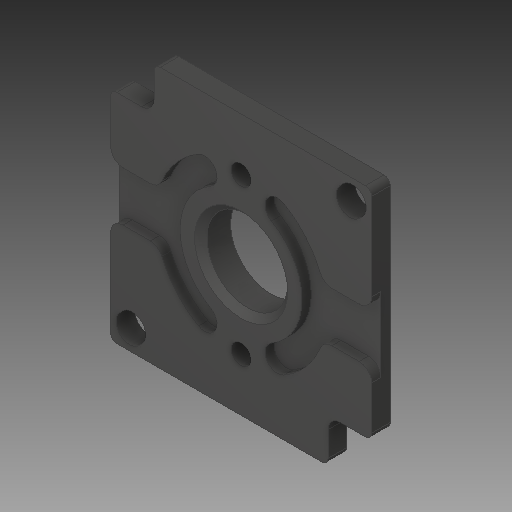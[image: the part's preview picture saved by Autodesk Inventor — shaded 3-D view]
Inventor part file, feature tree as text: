
AUTODESK INVENTOR PART (.ipt)
format: ipt  version: 2018 (Build 220112000, 112)  size: 266,240 bytes
history: native  units: in
note: dims shown in document units (in); Inventor stores cm internally (conversion verified against a paired STEP export)
features: fillet x1
ambient origin geometry x8: Origin, YZ Plane, XZ Plane, XY Plane, X Axis, Y Axis, Z Axis, Center Point
bodies: Solid1 (feature_tree)
feature tree (1):
  fillet  "Fillet4"  [1 undecoded]
note: 1 required parameter value undecoded (feature->parameter linkage not recoverable at this tier; creation-order binding heuristic only, values carry confidence <= 0.55)
